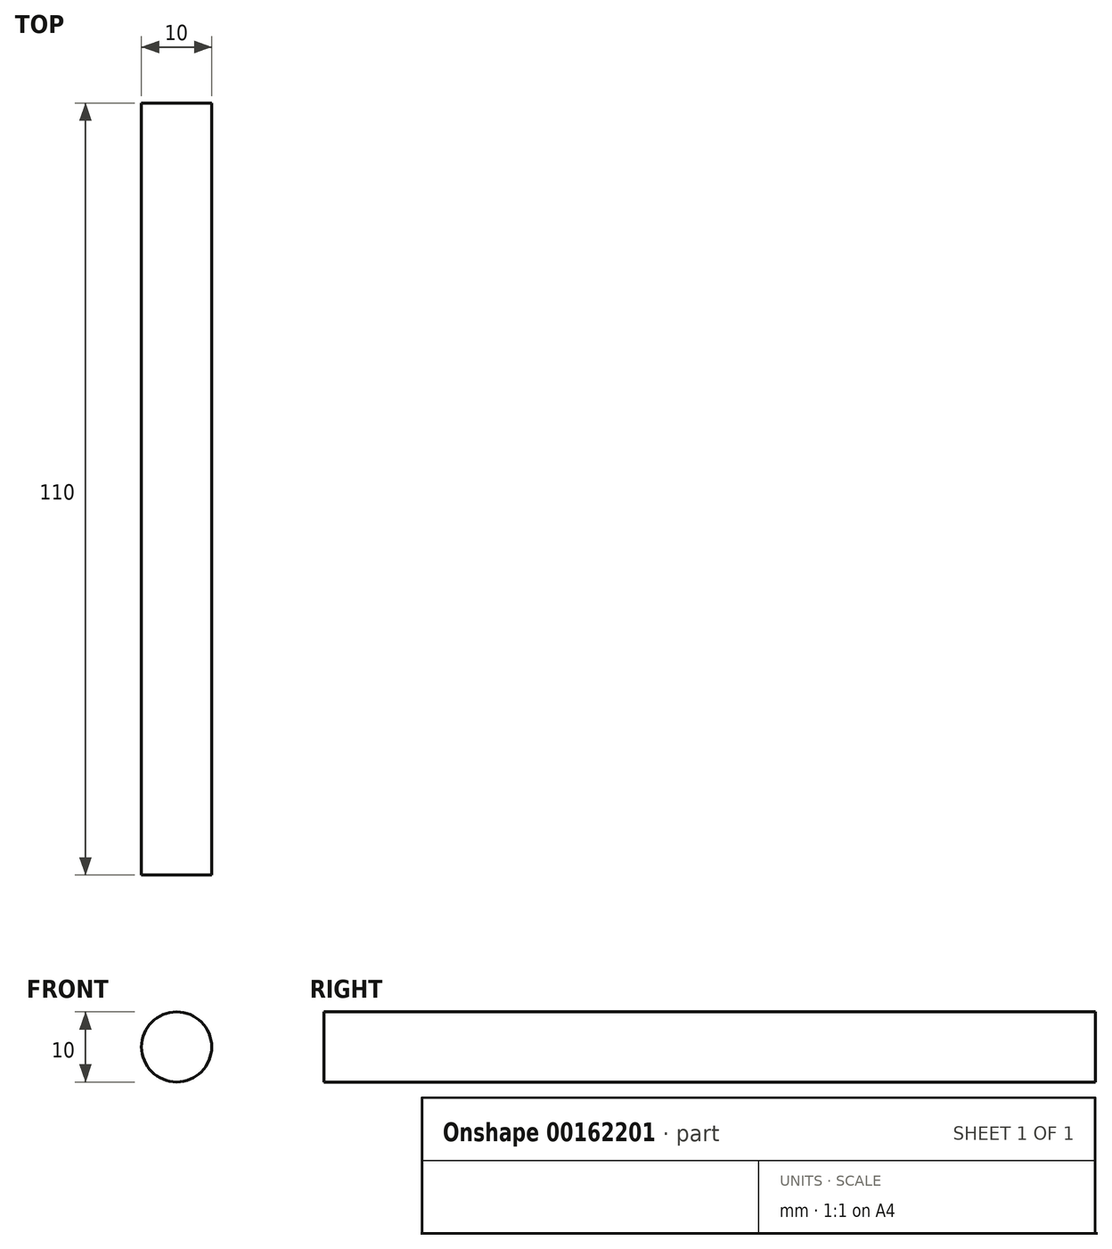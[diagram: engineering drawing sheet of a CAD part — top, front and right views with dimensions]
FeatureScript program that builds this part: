
annotation { "Feature Type Name" : "Feature", "Feature Type Description" : "" }
export const myFeature = defineFeature(function(context is Context, id is Id, definition is map)
    precondition{}
    {
        {
            var Q0;
            Q0=qCreatedBy(makeId("Front.planeOp"),FACE);
            var sketch = newSketch(context, id + "F0", { "sketchPlane" : qUnion([Q0])});
            skCircle(sketch, "E0", {"center": v(0, 0) * mm, "radius": 7.5 * mm});
            skCircle(sketch, "E1", {"center": v(0, 0) * mm, "radius": 5 * mm});
            skSolve(sketch);
        }
        {
            var Q0;
            Q0=makeQuery(id+"F0.imprint","IMPRINT",FACE,{"disambiguationData":[TD([[makeQuery(id+"F0.imprint","IMPRINT",EDGE,{"derivedFrom":sQuery(id+"F0.wireOp",EDGE,"E1")}),1.0]])]});
            extrude(context, id + "F1", {"entities" : qUnion([Q0]), "depth" : 10 * mm});
        }
        {
            var Q0;
            Q0=makeQuery(id+"F1.opExtrude","CAP_FACE",FACE,{"disambiguationData":[OSD([sQuery(id+"F0.wireOp",EDGE,"E1")])],"isStart":true});
            extrude(context, id + "F2", {"entities" : qUnion([Q0]), "operationType" : NewBodyOperationType.ADD, "depth" : 100 * mm});
        }
    });
